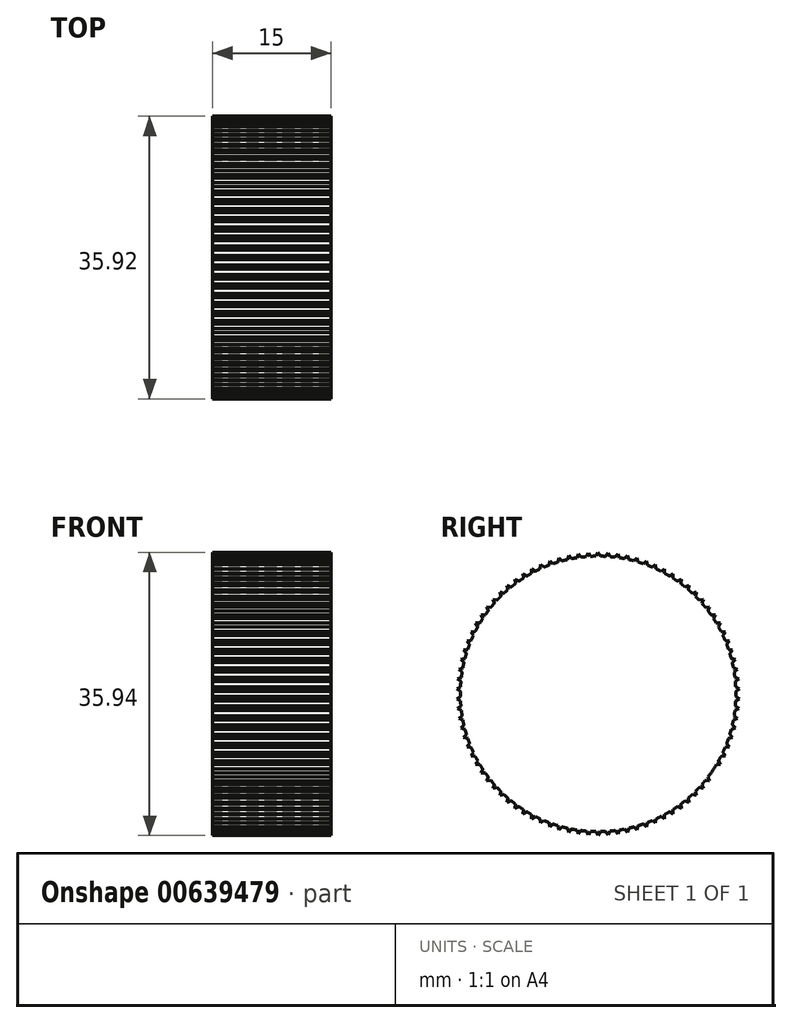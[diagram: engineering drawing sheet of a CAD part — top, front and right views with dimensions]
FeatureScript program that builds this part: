
annotation { "Feature Type Name" : "Feature", "Feature Type Description" : "" }
export const myFeature = defineFeature(function(context is Context, id is Id, definition is map)
    precondition{}
    {
        {
            var Q0;
            Q0=qCreatedBy(makeId("Right.planeOp"),FACE);
            var sketch = newSketch(context, id + "F0", { "sketchPlane" : qUnion([Q0])});
            skArc(sketch, "E0", {"start": v(-16.33, 6.3) * mm, "mid": v(-16.44, 5.99) * mm, "end": v(-16.56, 5.67) * mm});
            skLineSegment(sketch, "E1", {"start": v(0, 17.97) * mm, "end": v(-0.27, 17.5) * mm});
            skLineSegment(sketch, "E2.MirrorCS", {"start": v(0, 17.97) * mm, "end": v(0.27, 17.5) * mm});
            skLineSegment(sketch, "E3.1.0", {"start": v(-1.25, 17.92) * mm, "end": v(-0.95, 17.47) * mm});
            skLineSegment(sketch, "E3.1.1", {"start": v(-1.25, 17.92) * mm, "end": v(-1.5, 17.44) * mm});
            skLineSegment(sketch, "E3.2.0", {"start": v(-2.5, 17.8) * mm, "end": v(-2.17, 17.37) * mm});
            skLineSegment(sketch, "E3.2.1", {"start": v(-2.5, 17.8) * mm, "end": v(-2.7, 17.29) * mm});
            skLineSegment(sketch, "E4.2.3.0", {"start": v(-3.74, 17.58) * mm, "end": v(-3.37, 17.17) * mm});
            skLineSegment(sketch, "E4.3.3.0", {"start": v(-3.74, 17.58) * mm, "end": v(-3.9, 17.06) * mm});
            skLineSegment(sketch, "E4.2.4.0", {"start": v(-4.95, 17.27) * mm, "end": v(-4.56, 16.9) * mm});
            skLineSegment(sketch, "E4.3.4.0", {"start": v(-4.95, 17.27) * mm, "end": v(-5.08, 16.75) * mm});
            skLineSegment(sketch, "E4.2.5.0", {"start": v(-6.15, 16.88) * mm, "end": v(-5.73, 16.54) * mm});
            skLineSegment(sketch, "E4.3.5.0", {"start": v(-6.15, 16.88) * mm, "end": v(-6.24, 16.35) * mm});
            skLineSegment(sketch, "E5.2.6.0", {"start": v(-7.3, 16.41) * mm, "end": v(-6.87, 16.1) * mm});
            skLineSegment(sketch, "E5.3.6.0", {"start": v(-7.3, 16.41) * mm, "end": v(-7.36, 15.87) * mm});
            skLineSegment(sketch, "E5.2.7.0", {"start": v(-8.44, 15.86) * mm, "end": v(-7.98, 15.58) * mm});
            skLineSegment(sketch, "E5.3.7.0", {"start": v(-8.44, 15.86) * mm, "end": v(-8.45, 15.32) * mm});
            skLineSegment(sketch, "E5.2.8.0", {"start": v(-9.52, 15.24) * mm, "end": v(-9.04, 14.98) * mm});
            skLineSegment(sketch, "E5.3.8.0", {"start": v(-9.52, 15.24) * mm, "end": v(-9.5, 14.7) * mm});
            skLineSegment(sketch, "E5.2.9.0", {"start": v(-10.56, 14.54) * mm, "end": v(-10.07, 14.32) * mm});
            skLineSegment(sketch, "E5.3.9.0", {"start": v(-10.56, 14.54) * mm, "end": v(-10.5, 14) * mm});
            skLineSegment(sketch, "E6.2.10.0", {"start": v(-11.55, 13.76) * mm, "end": v(-11.04, 13.58) * mm});
            skLineSegment(sketch, "E6.3.10.0", {"start": v(-11.55, 13.76) * mm, "end": v(-11.46, 13.23) * mm});
            skLineSegment(sketch, "E6.2.11.0", {"start": v(-12.48, 12.92) * mm, "end": v(-11.96, 12.78) * mm});
            skLineSegment(sketch, "E6.3.11.0", {"start": v(-12.48, 12.92) * mm, "end": v(-12.35, 12.4) * mm});
            skLineSegment(sketch, "E6.2.12.0", {"start": v(-13.35, 12.02) * mm, "end": v(-12.82, 11.9) * mm});
            skLineSegment(sketch, "E6.3.12.0", {"start": v(-13.35, 12.02) * mm, "end": v(-13.18, 11.5) * mm});
            skLineSegment(sketch, "E6.2.13.0", {"start": v(-14.16, 11.06) * mm, "end": v(-13.62, 10.99) * mm});
            skLineSegment(sketch, "E6.3.13.0", {"start": v(-14.16, 11.06) * mm, "end": v(-13.96, 10.56) * mm});
            skLineSegment(sketch, "E6.2.14.0", {"start": v(-14.9, 10.05) * mm, "end": v(-14.35, 10) * mm});
            skLineSegment(sketch, "E6.3.14.0", {"start": v(-14.9, 10.05) * mm, "end": v(-14.66, 9.56) * mm});
            skLineSegment(sketch, "E6.2.15.0", {"start": v(-15.56, 8.98) * mm, "end": v(-15.02, 8.98) * mm});
            skLineSegment(sketch, "E6.3.15.0", {"start": v(-15.56, 8.98) * mm, "end": v(-15.29, 8.51) * mm});
            skLineSegment(sketch, "E6.2.16.0", {"start": v(-16.15, 7.88) * mm, "end": v(-15.6, 7.91) * mm});
            skLineSegment(sketch, "E6.3.16.0", {"start": v(-16.15, 7.88) * mm, "end": v(-15.85, 7.43) * mm});
            skLineSegment(sketch, "E6.2.17.0", {"start": v(-16.66, 6.73) * mm, "end": v(-16.12, 6.8) * mm});
            skLineSegment(sketch, "E6.3.17.0", {"start": v(-16.66, 6.73) * mm, "end": v(-16.33, 6.3) * mm});
            skLineSegment(sketch, "E6.2.18.0", {"start": v(-17.09, 5.55) * mm, "end": v(-16.56, 5.67) * mm});
            skLineSegment(sketch, "E6.3.18.0", {"start": v(-17.09, 5.55) * mm, "end": v(-16.73, 5.15) * mm});
            skLineSegment(sketch, "E6.2.19.0", {"start": v(-17.43, 4.35) * mm, "end": v(-16.91, 4.5) * mm});
            skLineSegment(sketch, "E6.3.19.0", {"start": v(-17.43, 4.35) * mm, "end": v(-17.04, 3.97) * mm});
            skLineSegment(sketch, "E7.2.20.0", {"start": v(-17.7, 3.12) * mm, "end": v(-17.18, 3.3) * mm});
            skLineSegment(sketch, "E7.3.20.0", {"start": v(-17.7, 3.12) * mm, "end": v(-17.28, 2.77) * mm});
            skLineSegment(sketch, "E7.2.21.0", {"start": v(-17.87, 1.88) * mm, "end": v(-17.37, 2.1) * mm});
            skLineSegment(sketch, "E7.3.21.0", {"start": v(-17.87, 1.88) * mm, "end": v(-17.43, 1.56) * mm});
            skLineSegment(sketch, "E7.2.22.0", {"start": v(-17.96, 0.63) * mm, "end": v(-17.48, 0.88) * mm});
            skLineSegment(sketch, "E7.3.22.0", {"start": v(-17.96, 0.63) * mm, "end": v(-17.5, 0.34) * mm});
            skLineSegment(sketch, "E7.2.23.0", {"start": v(-17.96, -0.63) * mm, "end": v(-17.5, -0.34) * mm});
            skLineSegment(sketch, "E7.3.23.0", {"start": v(-17.96, -0.63) * mm, "end": v(-17.48, -0.88) * mm});
            skLineSegment(sketch, "E7.2.24.0", {"start": v(-17.87, -1.88) * mm, "end": v(-17.43, -1.56) * mm});
            skLineSegment(sketch, "E7.3.24.0", {"start": v(-17.87, -1.88) * mm, "end": v(-17.37, -2.1) * mm});
            skLineSegment(sketch, "E7.2.25.0", {"start": v(-17.7, -3.12) * mm, "end": v(-17.28, -2.77) * mm});
            skLineSegment(sketch, "E7.3.25.0", {"start": v(-17.7, -3.12) * mm, "end": v(-17.18, -3.3) * mm});
            skLineSegment(sketch, "E7.2.26.0", {"start": v(-17.43, -4.35) * mm, "end": v(-17.04, -3.97) * mm});
            skLineSegment(sketch, "E7.3.26.0", {"start": v(-17.43, -4.35) * mm, "end": v(-16.91, -4.5) * mm});
            skLineSegment(sketch, "E7.2.27.0", {"start": v(-17.09, -5.55) * mm, "end": v(-16.73, -5.15) * mm});
            skLineSegment(sketch, "E7.3.27.0", {"start": v(-17.09, -5.55) * mm, "end": v(-16.56, -5.67) * mm});
            skLineSegment(sketch, "E7.2.28.0", {"start": v(-16.66, -6.73) * mm, "end": v(-16.33, -6.3) * mm});
            skLineSegment(sketch, "E7.3.28.0", {"start": v(-16.66, -6.73) * mm, "end": v(-16.12, -6.8) * mm});
            skLineSegment(sketch, "E7.2.29.0", {"start": v(-16.15, -7.88) * mm, "end": v(-15.85, -7.43) * mm});
            skLineSegment(sketch, "E7.3.29.0", {"start": v(-16.15, -7.88) * mm, "end": v(-15.6, -7.91) * mm});
            skLineSegment(sketch, "E8.2.30.0", {"start": v(-15.56, -8.98) * mm, "end": v(-15.29, -8.51) * mm});
            skLineSegment(sketch, "E8.3.30.0", {"start": v(-15.56, -8.98) * mm, "end": v(-15.02, -8.98) * mm});
            skLineSegment(sketch, "E8.2.31.0", {"start": v(-14.9, -10.05) * mm, "end": v(-14.66, -9.56) * mm});
            skLineSegment(sketch, "E8.3.31.0", {"start": v(-14.9, -10.05) * mm, "end": v(-14.35, -10) * mm});
            skLineSegment(sketch, "E8.2.32.0", {"start": v(-14.16, -11.06) * mm, "end": v(-13.96, -10.56) * mm});
            skLineSegment(sketch, "E8.3.32.0", {"start": v(-14.16, -11.06) * mm, "end": v(-13.62, -10.99) * mm});
            skLineSegment(sketch, "E8.2.33.0", {"start": v(-13.35, -12.02) * mm, "end": v(-13.18, -11.5) * mm});
            skLineSegment(sketch, "E8.3.33.0", {"start": v(-13.35, -12.02) * mm, "end": v(-12.82, -11.9) * mm});
            skLineSegment(sketch, "E8.2.34.0", {"start": v(-12.48, -12.92) * mm, "end": v(-12.35, -12.4) * mm});
            skLineSegment(sketch, "E8.3.34.0", {"start": v(-12.48, -12.92) * mm, "end": v(-11.96, -12.78) * mm});
            skLineSegment(sketch, "E8.2.35.0", {"start": v(-11.55, -13.76) * mm, "end": v(-11.46, -13.23) * mm});
            skLineSegment(sketch, "E8.3.35.0", {"start": v(-11.55, -13.76) * mm, "end": v(-11.04, -13.58) * mm});
            skLineSegment(sketch, "E8.2.36.0", {"start": v(-10.56, -14.54) * mm, "end": v(-10.5, -14) * mm});
            skLineSegment(sketch, "E8.3.36.0", {"start": v(-10.56, -14.54) * mm, "end": v(-10.07, -14.32) * mm});
            skLineSegment(sketch, "E8.2.37.0", {"start": v(-9.52, -15.24) * mm, "end": v(-9.5, -14.7) * mm});
            skLineSegment(sketch, "E8.3.37.0", {"start": v(-9.52, -15.24) * mm, "end": v(-9.04, -14.98) * mm});
            skLineSegment(sketch, "E8.2.38.0", {"start": v(-8.44, -15.86) * mm, "end": v(-8.45, -15.32) * mm});
            skLineSegment(sketch, "E8.3.38.0", {"start": v(-8.44, -15.86) * mm, "end": v(-7.98, -15.58) * mm});
            skLineSegment(sketch, "E8.2.39.0", {"start": v(-7.3, -16.41) * mm, "end": v(-7.36, -15.87) * mm});
            skLineSegment(sketch, "E8.3.39.0", {"start": v(-7.3, -16.41) * mm, "end": v(-6.87, -16.1) * mm});
            skLineSegment(sketch, "E8.2.40.0", {"start": v(-6.15, -16.88) * mm, "end": v(-6.24, -16.35) * mm});
            skLineSegment(sketch, "E8.3.40.0", {"start": v(-6.15, -16.88) * mm, "end": v(-5.73, -16.54) * mm});
            skLineSegment(sketch, "E8.2.41.0", {"start": v(-4.95, -17.27) * mm, "end": v(-5.08, -16.75) * mm});
            skLineSegment(sketch, "E8.3.41.0", {"start": v(-4.95, -17.27) * mm, "end": v(-4.56, -16.9) * mm});
            skLineSegment(sketch, "E8.2.42.0", {"start": v(-3.74, -17.58) * mm, "end": v(-3.9, -17.06) * mm});
            skLineSegment(sketch, "E8.3.42.0", {"start": v(-3.74, -17.58) * mm, "end": v(-3.37, -17.17) * mm});
            skLineSegment(sketch, "E8.2.43.0", {"start": v(-2.5, -17.8) * mm, "end": v(-2.7, -17.29) * mm});
            skLineSegment(sketch, "E8.3.43.0", {"start": v(-2.5, -17.8) * mm, "end": v(-2.17, -17.37) * mm});
            skLineSegment(sketch, "E8.2.44.0", {"start": v(-1.25, -17.92) * mm, "end": v(-1.5, -17.44) * mm});
            skLineSegment(sketch, "E8.3.44.0", {"start": v(-1.25, -17.92) * mm, "end": v(-0.95, -17.47) * mm});
            skLineSegment(sketch, "E8.2.45.0", {"start": v(0, -17.97) * mm, "end": v(-0.27, -17.5) * mm});
            skLineSegment(sketch, "E8.3.45.0", {"start": v(0, -17.97) * mm, "end": v(0.27, -17.5) * mm});
            skLineSegment(sketch, "E8.2.46.0", {"start": v(1.25, -17.92) * mm, "end": v(0.95, -17.47) * mm});
            skLineSegment(sketch, "E8.3.46.0", {"start": v(1.25, -17.92) * mm, "end": v(1.5, -17.44) * mm});
            skLineSegment(sketch, "E8.2.47.0", {"start": v(2.5, -17.8) * mm, "end": v(2.17, -17.37) * mm});
            skLineSegment(sketch, "E8.3.47.0", {"start": v(2.5, -17.8) * mm, "end": v(2.7, -17.29) * mm});
            skLineSegment(sketch, "E8.2.48.0", {"start": v(3.74, -17.58) * mm, "end": v(3.37, -17.17) * mm});
            skLineSegment(sketch, "E8.3.48.0", {"start": v(3.74, -17.58) * mm, "end": v(3.9, -17.06) * mm});
            skLineSegment(sketch, "E8.2.49.0", {"start": v(4.95, -17.27) * mm, "end": v(4.56, -16.9) * mm});
            skLineSegment(sketch, "E8.3.49.0", {"start": v(4.95, -17.27) * mm, "end": v(5.08, -16.75) * mm});
            skLineSegment(sketch, "E9.2.50.0", {"start": v(6.15, -16.88) * mm, "end": v(5.73, -16.54) * mm});
            skLineSegment(sketch, "E9.3.50.0", {"start": v(6.15, -16.88) * mm, "end": v(6.24, -16.35) * mm});
            skLineSegment(sketch, "E9.2.51.0", {"start": v(7.3, -16.41) * mm, "end": v(6.87, -16.1) * mm});
            skLineSegment(sketch, "E9.3.51.0", {"start": v(7.3, -16.41) * mm, "end": v(7.36, -15.87) * mm});
            skLineSegment(sketch, "E9.2.52.0", {"start": v(8.44, -15.86) * mm, "end": v(7.98, -15.58) * mm});
            skLineSegment(sketch, "E9.3.52.0", {"start": v(8.44, -15.86) * mm, "end": v(8.45, -15.32) * mm});
            skLineSegment(sketch, "E9.2.53.0", {"start": v(9.52, -15.24) * mm, "end": v(9.04, -14.98) * mm});
            skLineSegment(sketch, "E9.3.53.0", {"start": v(9.52, -15.24) * mm, "end": v(9.5, -14.7) * mm});
            skLineSegment(sketch, "E9.2.54.0", {"start": v(10.56, -14.54) * mm, "end": v(10.07, -14.32) * mm});
            skLineSegment(sketch, "E9.3.54.0", {"start": v(10.56, -14.54) * mm, "end": v(10.5, -14) * mm});
            skLineSegment(sketch, "E9.2.55.0", {"start": v(11.55, -13.76) * mm, "end": v(11.04, -13.58) * mm});
            skLineSegment(sketch, "E9.3.55.0", {"start": v(11.55, -13.76) * mm, "end": v(11.46, -13.23) * mm});
            skLineSegment(sketch, "E9.2.56.0", {"start": v(12.48, -12.92) * mm, "end": v(11.96, -12.78) * mm});
            skLineSegment(sketch, "E9.3.56.0", {"start": v(12.48, -12.92) * mm, "end": v(12.35, -12.4) * mm});
            skLineSegment(sketch, "E9.2.57.0", {"start": v(13.35, -12.02) * mm, "end": v(12.82, -11.9) * mm});
            skLineSegment(sketch, "E9.3.57.0", {"start": v(13.35, -12.02) * mm, "end": v(13.18, -11.5) * mm});
            skLineSegment(sketch, "E9.2.58.0", {"start": v(14.16, -11.06) * mm, "end": v(13.62, -10.99) * mm});
            skLineSegment(sketch, "E9.3.58.0", {"start": v(14.16, -11.06) * mm, "end": v(13.96, -10.56) * mm});
            skLineSegment(sketch, "E9.2.59.0", {"start": v(14.9, -10.05) * mm, "end": v(14.35, -10) * mm});
            skLineSegment(sketch, "E9.3.59.0", {"start": v(14.9, -10.05) * mm, "end": v(14.66, -9.56) * mm});
            skLineSegment(sketch, "E10.2.60.0", {"start": v(15.56, -8.98) * mm, "end": v(15.02, -8.98) * mm});
            skLineSegment(sketch, "E10.3.60.0", {"start": v(15.56, -8.98) * mm, "end": v(15.29, -8.51) * mm});
            skLineSegment(sketch, "E10.2.61.0", {"start": v(16.15, -7.88) * mm, "end": v(15.6, -7.91) * mm});
            skLineSegment(sketch, "E10.3.61.0", {"start": v(16.15, -7.88) * mm, "end": v(15.85, -7.43) * mm});
            skLineSegment(sketch, "E10.2.62.0", {"start": v(16.66, -6.73) * mm, "end": v(16.12, -6.8) * mm});
            skLineSegment(sketch, "E10.3.62.0", {"start": v(16.66, -6.73) * mm, "end": v(16.33, -6.3) * mm});
            skLineSegment(sketch, "E10.2.63.0", {"start": v(17.09, -5.55) * mm, "end": v(16.56, -5.67) * mm});
            skLineSegment(sketch, "E10.3.63.0", {"start": v(17.09, -5.55) * mm, "end": v(16.73, -5.15) * mm});
            skLineSegment(sketch, "E10.2.64.0", {"start": v(17.43, -4.35) * mm, "end": v(16.91, -4.5) * mm});
            skLineSegment(sketch, "E10.3.64.0", {"start": v(17.43, -4.35) * mm, "end": v(17.04, -3.97) * mm});
            skLineSegment(sketch, "E10.2.65.0", {"start": v(17.7, -3.12) * mm, "end": v(17.18, -3.3) * mm});
            skLineSegment(sketch, "E10.3.65.0", {"start": v(17.7, -3.12) * mm, "end": v(17.28, -2.77) * mm});
            skLineSegment(sketch, "E10.2.66.0", {"start": v(17.87, -1.88) * mm, "end": v(17.37, -2.1) * mm});
            skLineSegment(sketch, "E10.3.66.0", {"start": v(17.87, -1.88) * mm, "end": v(17.43, -1.56) * mm});
            skLineSegment(sketch, "E10.2.67.0", {"start": v(17.96, -0.63) * mm, "end": v(17.48, -0.88) * mm});
            skLineSegment(sketch, "E10.3.67.0", {"start": v(17.96, -0.63) * mm, "end": v(17.5, -0.34) * mm});
            skLineSegment(sketch, "E10.2.68.0", {"start": v(17.96, 0.63) * mm, "end": v(17.5, 0.34) * mm});
            skLineSegment(sketch, "E10.3.68.0", {"start": v(17.96, 0.63) * mm, "end": v(17.48, 0.88) * mm});
            skLineSegment(sketch, "E10.2.69.0", {"start": v(17.87, 1.88) * mm, "end": v(17.43, 1.56) * mm});
            skLineSegment(sketch, "E10.3.69.0", {"start": v(17.87, 1.88) * mm, "end": v(17.37, 2.1) * mm});
            skLineSegment(sketch, "E10.2.70.0", {"start": v(17.7, 3.12) * mm, "end": v(17.28, 2.77) * mm});
            skLineSegment(sketch, "E10.3.70.0", {"start": v(17.7, 3.12) * mm, "end": v(17.18, 3.3) * mm});
            skLineSegment(sketch, "E10.2.71.0", {"start": v(17.43, 4.35) * mm, "end": v(17.04, 3.97) * mm});
            skLineSegment(sketch, "E10.3.71.0", {"start": v(17.43, 4.35) * mm, "end": v(16.91, 4.5) * mm});
            skLineSegment(sketch, "E10.2.72.0", {"start": v(17.09, 5.55) * mm, "end": v(16.73, 5.15) * mm});
            skLineSegment(sketch, "E10.3.72.0", {"start": v(17.09, 5.55) * mm, "end": v(16.56, 5.67) * mm});
            skLineSegment(sketch, "E10.2.73.0", {"start": v(16.66, 6.73) * mm, "end": v(16.33, 6.3) * mm});
            skLineSegment(sketch, "E10.3.73.0", {"start": v(16.66, 6.73) * mm, "end": v(16.12, 6.8) * mm});
            skLineSegment(sketch, "E10.2.74.0", {"start": v(16.15, 7.88) * mm, "end": v(15.85, 7.43) * mm});
            skLineSegment(sketch, "E10.3.74.0", {"start": v(16.15, 7.88) * mm, "end": v(15.6, 7.91) * mm});
            skLineSegment(sketch, "E10.2.75.0", {"start": v(15.56, 8.98) * mm, "end": v(15.29, 8.51) * mm});
            skLineSegment(sketch, "E10.3.75.0", {"start": v(15.56, 8.98) * mm, "end": v(15.02, 8.98) * mm});
            skLineSegment(sketch, "E10.2.76.0", {"start": v(14.9, 10.05) * mm, "end": v(14.66, 9.56) * mm});
            skLineSegment(sketch, "E10.3.76.0", {"start": v(14.9, 10.05) * mm, "end": v(14.35, 10) * mm});
            skLineSegment(sketch, "E10.2.77.0", {"start": v(14.16, 11.06) * mm, "end": v(13.96, 10.56) * mm});
            skLineSegment(sketch, "E10.3.77.0", {"start": v(14.16, 11.06) * mm, "end": v(13.62, 10.99) * mm});
            skLineSegment(sketch, "E10.2.78.0", {"start": v(13.35, 12.02) * mm, "end": v(13.18, 11.5) * mm});
            skLineSegment(sketch, "E10.3.78.0", {"start": v(13.35, 12.02) * mm, "end": v(12.82, 11.9) * mm});
            skLineSegment(sketch, "E10.2.79.0", {"start": v(12.48, 12.92) * mm, "end": v(12.35, 12.4) * mm});
            skLineSegment(sketch, "E10.3.79.0", {"start": v(12.48, 12.92) * mm, "end": v(11.96, 12.78) * mm});
            skLineSegment(sketch, "E10.2.80.0", {"start": v(11.55, 13.76) * mm, "end": v(11.46, 13.23) * mm});
            skLineSegment(sketch, "E10.3.80.0", {"start": v(11.55, 13.76) * mm, "end": v(11.04, 13.58) * mm});
            skLineSegment(sketch, "E10.2.81.0", {"start": v(10.56, 14.54) * mm, "end": v(10.5, 14) * mm});
            skLineSegment(sketch, "E10.3.81.0", {"start": v(10.56, 14.54) * mm, "end": v(10.07, 14.32) * mm});
            skLineSegment(sketch, "E10.2.82.0", {"start": v(9.52, 15.24) * mm, "end": v(9.5, 14.7) * mm});
            skLineSegment(sketch, "E10.3.82.0", {"start": v(9.52, 15.24) * mm, "end": v(9.04, 14.98) * mm});
            skLineSegment(sketch, "E10.2.83.0", {"start": v(8.44, 15.86) * mm, "end": v(8.45, 15.32) * mm});
            skLineSegment(sketch, "E10.3.83.0", {"start": v(8.44, 15.86) * mm, "end": v(7.98, 15.58) * mm});
            skLineSegment(sketch, "E10.2.84.0", {"start": v(7.3, 16.41) * mm, "end": v(7.36, 15.87) * mm});
            skLineSegment(sketch, "E10.3.84.0", {"start": v(7.3, 16.41) * mm, "end": v(6.87, 16.1) * mm});
            skLineSegment(sketch, "E10.2.85.0", {"start": v(6.15, 16.88) * mm, "end": v(6.24, 16.35) * mm});
            skLineSegment(sketch, "E10.3.85.0", {"start": v(6.15, 16.88) * mm, "end": v(5.73, 16.54) * mm});
            skLineSegment(sketch, "E10.2.86.0", {"start": v(4.95, 17.27) * mm, "end": v(5.08, 16.75) * mm});
            skLineSegment(sketch, "E10.3.86.0", {"start": v(4.95, 17.27) * mm, "end": v(4.56, 16.9) * mm});
            skLineSegment(sketch, "E10.2.87.0", {"start": v(3.74, 17.58) * mm, "end": v(3.9, 17.06) * mm});
            skLineSegment(sketch, "E10.3.87.0", {"start": v(3.74, 17.58) * mm, "end": v(3.37, 17.17) * mm});
            skLineSegment(sketch, "E10.2.88.0", {"start": v(2.5, 17.8) * mm, "end": v(2.7, 17.29) * mm});
            skLineSegment(sketch, "E10.3.88.0", {"start": v(2.5, 17.8) * mm, "end": v(2.17, 17.37) * mm});
            skLineSegment(sketch, "E10.2.89.0", {"start": v(1.25, 17.92) * mm, "end": v(1.5, 17.44) * mm});
            skLineSegment(sketch, "E10.3.89.0", {"start": v(1.25, 17.92) * mm, "end": v(0.95, 17.47) * mm});
            skArc(sketch, "E11.trimOffspring", {"start": v(-16.73, 5.15) * mm, "mid": v(-16.82, 4.82) * mm, "end": v(-16.91, 4.5) * mm});
            skArc(sketch, "E12.trimOffspring", {"start": v(-15.85, 7.43) * mm, "mid": v(-15.99, 7.12) * mm, "end": v(-16.12, 6.8) * mm});
            skArc(sketch, "E13.trimOffspring", {"start": v(-17.04, 3.97) * mm, "mid": v(-17.12, 3.64) * mm, "end": v(-17.18, 3.3) * mm});
            skArc(sketch, "E14.trimOffspring", {"start": v(-15.29, 8.51) * mm, "mid": v(-15.45, 8.22) * mm, "end": v(-15.6, 7.91) * mm});
            skArc(sketch, "E15.trimOffspring", {"start": v(-14.66, 9.56) * mm, "mid": v(-14.84, 9.27) * mm, "end": v(-15.02, 8.98) * mm});
            skArc(sketch, "E16.trimOffspring", {"start": v(-10.5, 14) * mm, "mid": v(-10.77, 13.8) * mm, "end": v(-11.04, 13.58) * mm});
            skArc(sketch, "E17.trimOffspring", {"start": v(-11.46, 13.23) * mm, "mid": v(-11.7, 13) * mm, "end": v(-11.96, 12.78) * mm});
            skArc(sketch, "E18.trimOffspring", {"start": v(-12.35, 12.4) * mm, "mid": v(-12.59, 12.16) * mm, "end": v(-12.82, 11.9) * mm});
            skArc(sketch, "E19.trimOffspring", {"start": v(-13.18, 11.5) * mm, "mid": v(-13.4, 11.25) * mm, "end": v(-13.62, 10.99) * mm});
            skArc(sketch, "E20.trimOffspring", {"start": v(-13.96, 10.56) * mm, "mid": v(-14.16, 10.29) * mm, "end": v(-14.35, 10) * mm});
            skArc(sketch, "E21.trimOffspring", {"start": v(-7.36, 15.87) * mm, "mid": v(-7.67, 15.73) * mm, "end": v(-7.98, 15.58) * mm});
            skArc(sketch, "E22.trimOffspring", {"start": v(-8.45, 15.32) * mm, "mid": v(-8.75, 15.16) * mm, "end": v(-9.04, 14.98) * mm});
            skArc(sketch, "E23.trimOffspring", {"start": v(-9.5, 14.7) * mm, "mid": v(-9.79, 14.5) * mm, "end": v(-10.07, 14.32) * mm});
            skArc(sketch, "E24.trimOffspring", {"start": v(-6.24, 16.35) * mm, "mid": v(-6.56, 16.23) * mm, "end": v(-6.87, 16.1) * mm});
            skArc(sketch, "E25.trimOffspring", {"start": v(-5.08, 16.75) * mm, "mid": v(-5.4, 16.64) * mm, "end": v(-5.73, 16.54) * mm});
            skArc(sketch, "E26.trimOffspring", {"start": v(-3.9, 17.06) * mm, "mid": v(-4.23, 16.98) * mm, "end": v(-4.56, 16.9) * mm});
            skArc(sketch, "E27.trimOffspring", {"start": v(-2.7, 17.29) * mm, "mid": v(-3.04, 17.23) * mm, "end": v(-3.37, 17.17) * mm});
            skArc(sketch, "E28.trimOffspring", {"start": v(-1.5, 17.44) * mm, "mid": v(-1.83, 17.4) * mm, "end": v(-2.17, 17.37) * mm});
            skArc(sketch, "E29.trimOffspring", {"start": v(0.95, 17.47) * mm, "mid": v(0.61, 17.49) * mm, "end": v(0.27, 17.5) * mm});
            skArc(sketch, "E30.trimOffspring", {"start": v(-0.27, 17.5) * mm, "mid": v(-0.61, 17.49) * mm, "end": v(-0.95, 17.47) * mm});
            skArc(sketch, "E31.trimOffspring", {"start": v(2.17, 17.37) * mm, "mid": v(1.83, 17.4) * mm, "end": v(1.5, 17.44) * mm});
            skArc(sketch, "E32.trimOffspring", {"start": v(3.37, 17.17) * mm, "mid": v(3.04, 17.23) * mm, "end": v(2.7, 17.29) * mm});
            skArc(sketch, "E33.trimOffspring", {"start": v(4.56, 16.9) * mm, "mid": v(4.23, 16.98) * mm, "end": v(3.9, 17.06) * mm});
            skArc(sketch, "E34.trimOffspring", {"start": v(5.73, 16.54) * mm, "mid": v(5.4, 16.64) * mm, "end": v(5.08, 16.75) * mm});
            skArc(sketch, "E35.trimOffspring", {"start": v(6.87, 16.1) * mm, "mid": v(6.56, 16.23) * mm, "end": v(6.24, 16.35) * mm});
            skArc(sketch, "E36.trimOffspring", {"start": v(7.98, 15.58) * mm, "mid": v(7.67, 15.73) * mm, "end": v(7.36, 15.87) * mm});
            skArc(sketch, "E37.trimOffspring", {"start": v(9.04, 14.98) * mm, "mid": v(8.75, 15.16) * mm, "end": v(8.45, 15.32) * mm});
            skArc(sketch, "E38.trimOffspring", {"start": v(10.07, 14.32) * mm, "mid": v(9.79, 14.5) * mm, "end": v(9.5, 14.7) * mm});
            skArc(sketch, "E39.trimOffspring", {"start": v(11.04, 13.58) * mm, "mid": v(10.77, 13.8) * mm, "end": v(10.5, 14) * mm});
            skArc(sketch, "E40.trimOffspring", {"start": v(11.96, 12.78) * mm, "mid": v(11.7, 13) * mm, "end": v(11.46, 13.23) * mm});
            skArc(sketch, "E41.trimOffspring", {"start": v(16.56, 5.67) * mm, "mid": v(16.44, 5.99) * mm, "end": v(16.33, 6.3) * mm});
            skArc(sketch, "E42.trimOffspring", {"start": v(16.12, 6.8) * mm, "mid": v(15.99, 7.12) * mm, "end": v(15.85, 7.43) * mm});
            skArc(sketch, "E43.trimOffspring", {"start": v(15.6, 7.91) * mm, "mid": v(15.45, 8.22) * mm, "end": v(15.29, 8.51) * mm});
            skArc(sketch, "E44.trimOffspring", {"start": v(16.91, 4.5) * mm, "mid": v(16.82, 4.82) * mm, "end": v(16.73, 5.15) * mm});
            skArc(sketch, "E45.trimOffspring", {"start": v(17.18, 3.3) * mm, "mid": v(17.12, 3.64) * mm, "end": v(17.04, 3.97) * mm});
            skArc(sketch, "E46.trimOffspring", {"start": v(17.37, 2.1) * mm, "mid": v(17.33, 2.44) * mm, "end": v(17.28, 2.77) * mm});
            skArc(sketch, "E47.trimOffspring", {"start": v(17.48, 0.88) * mm, "mid": v(17.46, 1.22) * mm, "end": v(17.43, 1.56) * mm});
            skArc(sketch, "E48.trimOffspring", {"start": v(12.82, 11.9) * mm, "mid": v(12.59, 12.16) * mm, "end": v(12.35, 12.4) * mm});
            skArc(sketch, "E49.trimOffspring", {"start": v(13.62, 10.99) * mm, "mid": v(13.4, 11.25) * mm, "end": v(13.18, 11.5) * mm});
            skArc(sketch, "E50.trimOffspring", {"start": v(14.35, 10) * mm, "mid": v(14.16, 10.29) * mm, "end": v(13.96, 10.56) * mm});
            skArc(sketch, "E51.trimOffspring", {"start": v(15.02, 8.98) * mm, "mid": v(14.84, 9.27) * mm, "end": v(14.66, 9.56) * mm});
            skArc(sketch, "E52.trimOffspring", {"start": v(13.18, -11.5) * mm, "mid": v(13.4, -11.25) * mm, "end": v(13.62, -10.99) * mm});
            skArc(sketch, "E53.trimOffspring", {"start": v(13.96, -10.56) * mm, "mid": v(14.5, -9.79) * mm, "end": v(15.02, -8.98) * mm});
            skArc(sketch, "E54.trimOffspring", {"start": v(12.35, -12.4) * mm, "mid": v(12.59, -12.16) * mm, "end": v(12.82, -11.9) * mm});
            skArc(sketch, "E55.trimOffspring", {"start": v(11.46, -13.23) * mm, "mid": v(11.7, -13) * mm, "end": v(11.96, -12.78) * mm});
            skArc(sketch, "E56.trimOffspring", {"start": v(10.5, -14) * mm, "mid": v(10.77, -13.8) * mm, "end": v(11.04, -13.58) * mm});
            skArc(sketch, "E57.trimOffspring", {"start": v(17.43, -1.56) * mm, "mid": v(17.46, -1.22) * mm, "end": v(17.48, -0.88) * mm});
            skArc(sketch, "E58.trimOffspring", {"start": v(17.5, -0.34) * mm, "mid": v(17.5, 0) * mm, "end": v(17.5, 0.34) * mm});
            skArc(sketch, "E59.trimOffspring", {"start": v(17.28, -2.77) * mm, "mid": v(17.33, -2.44) * mm, "end": v(17.37, -2.1) * mm});
            skArc(sketch, "E60.trimOffspring", {"start": v(17.04, -3.97) * mm, "mid": v(17.12, -3.64) * mm, "end": v(17.18, -3.3) * mm});
            skArc(sketch, "E61.trimOffspring", {"start": v(15.29, -8.51) * mm, "mid": v(15.45, -8.22) * mm, "end": v(15.6, -7.91) * mm});
            skArc(sketch, "E62.trimOffspring", {"start": v(15.85, -7.43) * mm, "mid": v(15.99, -7.12) * mm, "end": v(16.12, -6.8) * mm});
            skArc(sketch, "E63.trimOffspring", {"start": v(16.33, -6.3) * mm, "mid": v(16.44, -5.99) * mm, "end": v(16.56, -5.67) * mm});
            skArc(sketch, "E64.trimOffspring", {"start": v(16.73, -5.15) * mm, "mid": v(16.82, -4.82) * mm, "end": v(16.91, -4.5) * mm});
            skArc(sketch, "E65.trimOffspring", {"start": v(8.45, -15.32) * mm, "mid": v(8.75, -15.16) * mm, "end": v(9.04, -14.98) * mm});
            skArc(sketch, "E66.trimOffspring", {"start": v(9.5, -14.7) * mm, "mid": v(9.79, -14.5) * mm, "end": v(10.07, -14.32) * mm});
            skArc(sketch, "E67.trimOffspring", {"start": v(7.36, -15.87) * mm, "mid": v(7.67, -15.73) * mm, "end": v(7.98, -15.58) * mm});
            skArc(sketch, "E68.trimOffspring", {"start": v(6.24, -16.35) * mm, "mid": v(6.56, -16.23) * mm, "end": v(6.87, -16.1) * mm});
            skArc(sketch, "E69.trimOffspring", {"start": v(5.08, -16.75) * mm, "mid": v(5.4, -16.64) * mm, "end": v(5.73, -16.54) * mm});
            skArc(sketch, "E70.trimOffspring", {"start": v(3.9, -17.06) * mm, "mid": v(4.23, -16.98) * mm, "end": v(4.56, -16.9) * mm});
            skArc(sketch, "E71.trimOffspring", {"start": v(2.7, -17.29) * mm, "mid": v(3.04, -17.23) * mm, "end": v(3.37, -17.17) * mm});
            skArc(sketch, "E72.trimOffspring", {"start": v(0.27, -17.5) * mm, "mid": v(0.61, -17.49) * mm, "end": v(0.95, -17.47) * mm});
            skArc(sketch, "E73.trimOffspring", {"start": v(1.5, -17.44) * mm, "mid": v(1.83, -17.4) * mm, "end": v(2.17, -17.37) * mm});
            skArc(sketch, "E74.trimOffspring", {"start": v(-0.95, -17.47) * mm, "mid": v(-0.61, -17.49) * mm, "end": v(-0.27, -17.5) * mm});
            skArc(sketch, "E75.trimOffspring", {"start": v(-2.17, -17.37) * mm, "mid": v(-1.83, -17.4) * mm, "end": v(-1.5, -17.44) * mm});
            skArc(sketch, "E76.trimOffspring", {"start": v(-3.37, -17.17) * mm, "mid": v(-3.04, -17.23) * mm, "end": v(-2.7, -17.29) * mm});
            skArc(sketch, "E77.trimOffspring", {"start": v(-4.56, -16.9) * mm, "mid": v(-4.23, -16.98) * mm, "end": v(-3.9, -17.06) * mm});
            skArc(sketch, "E78.trimOffspring", {"start": v(-5.73, -16.54) * mm, "mid": v(-5.4, -16.64) * mm, "end": v(-5.08, -16.75) * mm});
            skArc(sketch, "E79.trimOffspring", {"start": v(-6.87, -16.1) * mm, "mid": v(-6.56, -16.23) * mm, "end": v(-6.24, -16.35) * mm});
            skArc(sketch, "E80.trimOffspring", {"start": v(-7.98, -15.58) * mm, "mid": v(-7.67, -15.73) * mm, "end": v(-7.36, -15.87) * mm});
            skArc(sketch, "E81.trimOffspring", {"start": v(-9.04, -14.98) * mm, "mid": v(-8.75, -15.16) * mm, "end": v(-8.45, -15.32) * mm});
            skArc(sketch, "E82.trimOffspring", {"start": v(-11.96, -12.78) * mm, "mid": v(-11.7, -13) * mm, "end": v(-11.46, -13.23) * mm});
            skArc(sketch, "E83.trimOffspring", {"start": v(-12.82, -11.9) * mm, "mid": v(-12.59, -12.16) * mm, "end": v(-12.35, -12.4) * mm});
            skArc(sketch, "E84.trimOffspring", {"start": v(-13.62, -10.99) * mm, "mid": v(-13.4, -11.25) * mm, "end": v(-13.18, -11.5) * mm});
            skArc(sketch, "E85.trimOffspring", {"start": v(-14.35, -10) * mm, "mid": v(-14.16, -10.29) * mm, "end": v(-13.96, -10.56) * mm});
            skArc(sketch, "E86.trimOffspring", {"start": v(-15.02, -8.98) * mm, "mid": v(-14.84, -9.27) * mm, "end": v(-14.66, -9.56) * mm});
            skArc(sketch, "E87.trimOffspring", {"start": v(-15.6, -7.91) * mm, "mid": v(-15.45, -8.22) * mm, "end": v(-15.29, -8.51) * mm});
            skArc(sketch, "E88.trimOffspring", {"start": v(-16.12, -6.8) * mm, "mid": v(-15.99, -7.12) * mm, "end": v(-15.85, -7.43) * mm});
            skArc(sketch, "E89.trimOffspring", {"start": v(-16.56, -5.67) * mm, "mid": v(-16.44, -5.99) * mm, "end": v(-16.33, -6.3) * mm});
            skArc(sketch, "E90.trimOffspring", {"start": v(-16.91, -4.5) * mm, "mid": v(-16.82, -4.82) * mm, "end": v(-16.73, -5.15) * mm});
            skArc(sketch, "E91.trimOffspring", {"start": v(-17.18, -3.3) * mm, "mid": v(-17.12, -3.64) * mm, "end": v(-17.04, -3.97) * mm});
            skArc(sketch, "E92.trimOffspring", {"start": v(-17.37, -2.1) * mm, "mid": v(-17.33, -2.44) * mm, "end": v(-17.28, -2.77) * mm});
            skArc(sketch, "E93.trimOffspring", {"start": v(-17.5, 0.34) * mm, "mid": v(-17.5, 0) * mm, "end": v(-17.5, -0.34) * mm});
            skArc(sketch, "E94.trimOffspring", {"start": v(-17.48, -0.88) * mm, "mid": v(-17.46, -1.22) * mm, "end": v(-17.43, -1.56) * mm});
            skArc(sketch, "E95.trimOffspring", {"start": v(-17.43, 1.56) * mm, "mid": v(-17.46, 1.22) * mm, "end": v(-17.48, 0.88) * mm});
            skArc(sketch, "E96.trimOffspring", {"start": v(-17.28, 2.77) * mm, "mid": v(-17.33, 2.44) * mm, "end": v(-17.37, 2.1) * mm});
            skArc(sketch, "E97.trimOffspring", {"start": v(-10.07, -14.32) * mm, "mid": v(-9.79, -14.5) * mm, "end": v(-9.5, -14.7) * mm});
            skArc(sketch, "E98.trimOffspring", {"start": v(-11.04, -13.58) * mm, "mid": v(-10.77, -13.8) * mm, "end": v(-10.5, -14) * mm});
            skSolve(sketch);
        }
        {
            var Q0;
            Q0=makeQuery(id+"F0.imprint","IMPRINT",FACE,{"disambiguationData":[TD([[makeQuery(id+"F0.imprint","IMPRINT",EDGE,{"derivedFrom":sQuery(id+"F0.wireOp",EDGE,"E0")}),1.0]])]});
            extrude(context, id + "F1", {"entities" : qUnion([Q0]), "depth" : 15 * mm, "offsetDistance" : 25 * mm});
        }
    });
